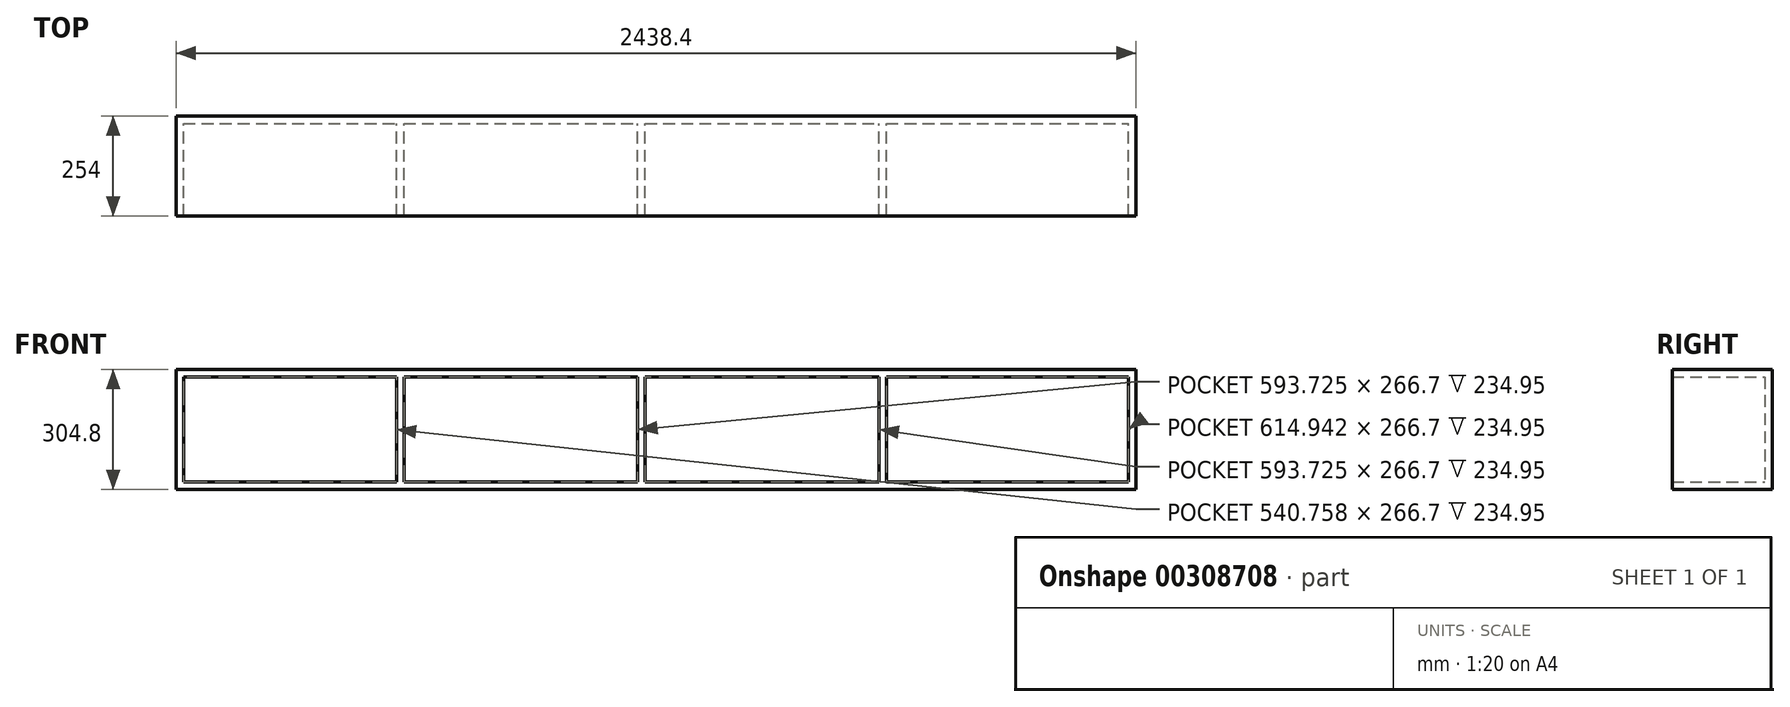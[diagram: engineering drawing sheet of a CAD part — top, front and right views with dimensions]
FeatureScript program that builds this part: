
annotation { "Feature Type Name" : "Feature", "Feature Type Description" : "" }
export const myFeature = defineFeature(function(context is Context, id is Id, definition is map)
    precondition{}
    {
        {
            var Q0;
            Q0=qCreatedBy(makeId("Front.planeOp"),FACE);
            var sketch = newSketch(context, id + "F0", { "sketchPlane" : qUnion([Q0])});
            skLineSegment(sketch, "E0.bottom", {"start": v(0, 0) * mm, "end": v(2438.4, 0) * mm});
            skLineSegment(sketch, "E0.top", {"start": v(0, -304.8) * mm, "end": v(2438.4, -304.8) * mm});
            skLineSegment(sketch, "E0.left", {"start": v(0, 0) * mm, "end": v(0, -304.8) * mm});
            skLineSegment(sketch, "E0.right", {"start": v(2438.4, 0) * mm, "end": v(2438.4, -304.8) * mm});
            skLineSegment(sketch, "E1.0", {"start": v(19.05, -19.05) * mm, "end": v(2419.35, -19.05) * mm});
            skLineSegment(sketch, "E1.1", {"start": v(19.05, -19.05) * mm, "end": v(19.05, -285.75) * mm});
            skLineSegment(sketch, "E1.2", {"start": v(19.05, -285.75) * mm, "end": v(2419.35, -285.75) * mm});
            skLineSegment(sketch, "E1.3", {"start": v(2419.35, -19.05) * mm, "end": v(2419.35, -285.75) * mm});
            skSolve(sketch);
        }
        {
            var Q0;
            Q0 = qSketchRegion(id + "F0", true);
            extrude(context, id + "F1", {"entities" : qUnion([Q0]), "depth" : 254 * mm});
        }
        {
            var Q0;
            Q0=qCreatedBy(makeId("Front.planeOp"),FACE);
            var sketch = newSketch(context, id + "F2", { "sketchPlane" : qUnion([Q0])});
            skLineSegment(sketch, "E2.0", {"start": v(0, 0) * mm, "end": v(2438.4, 0) * mm});
            skLineSegment(sketch, "E3.0", {"start": v(0, 0) * mm, "end": v(0, -304.8) * mm});
            skLineSegment(sketch, "E4.0", {"start": v(0, -304.8) * mm, "end": v(2438.4, -304.8) * mm});
            skLineSegment(sketch, "E5.0", {"start": v(2438.4, 0) * mm, "end": v(2438.4, -304.8) * mm});
            skSolve(sketch);
        }
        {
            var Q0;
            Q0 = qSketchRegion(id + "F2", true);
            extrude(context, id + "F3", {"entities" : qUnion([Q0]), "operationType" : NewBodyOperationType.ADD, "depth" : 19.05 * mm});
        }
        {
            var Q0;
            Q0=makeQuery(id+"F3.opExtrude","CAP_FACE",FACE,{"disambiguationData":[OSD([sQuery(id+"F2.wireOp",EDGE,"E2.0"),sQuery(id+"F2.wireOp",EDGE,"E3.0"),sQuery(id+"F2.wireOp",EDGE,"E4.0"),sQuery(id+"F2.wireOp",EDGE,"E5.0")])],"isStart":false});
            var sketch = newSketch(context, id + "F4", { "sketchPlane" : qUnion([Q0])});
            skLineSegment(sketch, "E6.bottom", {"start": v(1172.58, -19.05) * mm, "end": v(1191.63, -19.05) * mm});
            skLineSegment(sketch, "E6.top", {"start": v(1172.58, -285.75) * mm, "end": v(1191.63, -285.75) * mm});
            skLineSegment(sketch, "E6.left", {"start": v(1172.58, -19.05) * mm, "end": v(1172.58, -285.75) * mm});
            skLineSegment(sketch, "E6.right", {"start": v(1191.63, -19.05) * mm, "end": v(1191.63, -285.75) * mm});
            skLineSegment(sketch, "E7.bottom", {"start": v(1785.36, -19.05) * mm, "end": v(1804.4, -19.05) * mm});
            skLineSegment(sketch, "E7.top", {"start": v(1785.36, -285.75) * mm, "end": v(1804.4, -285.75) * mm});
            skLineSegment(sketch, "E7.left", {"start": v(1785.36, -19.05) * mm, "end": v(1785.36, -285.75) * mm});
            skLineSegment(sketch, "E7.right", {"start": v(1804.4, -19.05) * mm, "end": v(1804.4, -285.75) * mm});
            skLineSegment(sketch, "E8.bottom", {"start": v(559.8, -19.05) * mm, "end": v(578.86, -19.05) * mm});
            skLineSegment(sketch, "E8.top", {"start": v(559.8, -285.75) * mm, "end": v(578.86, -285.75) * mm});
            skLineSegment(sketch, "E8.left", {"start": v(559.8, -19.05) * mm, "end": v(559.8, -285.75) * mm});
            skLineSegment(sketch, "E8.right", {"start": v(578.86, -19.05) * mm, "end": v(578.86, -285.75) * mm});
            skSolve(sketch);
        }
        {
            var Q0;
            Q0 = qSketchRegion(id + "F4", true);
            extrude(context, id + "F5", {"entities" : qUnion([Q0]), "operationType" : NewBodyOperationType.ADD, "depth" : 234.95 * mm});
        }
    });
